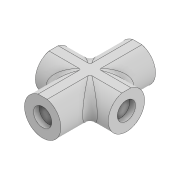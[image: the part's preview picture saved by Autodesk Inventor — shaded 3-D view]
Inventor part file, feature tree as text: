
AUTODESK INVENTOR PART (.ipt)
format: ipt  version: 2020 (Build 240168000, 168)  size: 398,848 bytes
history: native  units: mm
features: extrude x5, sketch x5, mirror x2, fillet x1, plane x1
ambient origin geometry x8: Origin, YZ Plane, XZ Plane, XY Plane, X Axis, Y Axis, Z Axis, Center Point
bodies: Solid1 (feature_tree)
feature tree (14):
  extrude  "Extrusion1"  Depth=13.0mm TaperAngle=0.0deg
  extrude  "Extrusion2"  Depth=0.8mm TaperAngle=0.0deg
  mirror  "Mirror1"
  extrude  "Extrusion3"  Depth=10.0mm TaperAngle=0.0deg
  extrude  "Extrusion4"  Depth=0.8mm TaperAngle=0.0deg
  mirror  "Mirror2"
  fillet  "Fillet1"  Radius=1.0mm
  extrude  "Extrusion5"  [1 undecoded]
  sketch  "Sketch1"  dims[d0=5.0mm d1=13.0mm d2=0.0mm]
  sketch  "Sketch2"  dims[d3=2.5mm d4=0.8mm d5=0.0mm]
  plane  "Work Plane1"
  sketch  "Sketch3"  dims[d6=5.0mm d7=10.0mm d8=0.0mm]
  sketch  "Sketch4"  dims[d9=2.5mm d10=0.8mm d11=0.0mm d12=1.0mm]
  sketch  "Sketch5"  dims[d13=0.0mm d14=0.0mm]
note: 1 required parameter value undecoded (feature->parameter linkage not recoverable at this tier; creation-order binding heuristic only, values carry confidence <= 0.55)
